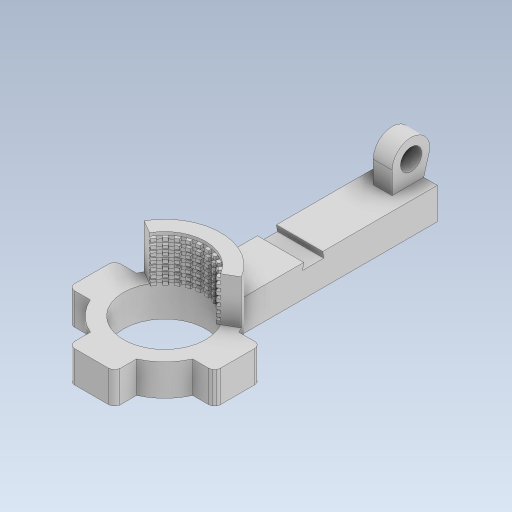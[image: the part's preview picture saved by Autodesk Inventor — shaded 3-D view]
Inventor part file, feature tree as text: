
AUTODESK INVENTOR PART (.ipt)
format: ipt  version: 2023 (Build 270158000, 158)  size: 567,808 bytes
history: native  units: in
note: dims shown in document units (in); Inventor stores cm internally (conversion verified against a paired STEP export)
features: sketch x10, extrude x8, revolve x1, hole x1, mirror x1, projected_geometry x1
ambient origin geometry x8: Origin, YZ Plane, XZ Plane, XY Plane, X Axis, Y Axis, Z Axis, Center Point
bodies: Solid1 (feature_tree)
feature tree (22):
  extrude  "Extrusion1"  Depth=0.3937in TaperAngle=0.0deg
  extrude  "Extrusion2"  Depth=0.5512in TaperAngle=0.0deg
  extrude  "Extrusion3"  Depth=0.0394in TaperAngle=120.0deg
  revolve  "Revolution1"  [1 undecoded]
  extrude  "Extrusion4"  Depth=0.1969in TaperAngle=0.0deg
  extrude  "Extrusion5"  Depth=0.2362in
  extrude  "Extrusion6"  Depth=0.0787in
  hole  "Hole1"  [1 undecoded]
  mirror  "Mirror1"
  extrude  "Extrusion7"  Depth=0.2756in
  extrude  "Extrusion8"  Depth=0.0787in
  sketch  "Sketch1"  dims[d0=1.0236in d1=0.3937in d2=0.0in]
  sketch  "Sketch2"  dims[d3=120.0deg d4=0.5512in d5=0.0in]
  sketch  "Sketch3"  dims[d6=0.0394in d7=7.874in d9=120.0deg]
  sketch  "Sketch4"  dims[d11=0.3937in d12=0.0in d14=5.5118in d16=0.0394in d17=0.3937in d19=0.3937in]
  sketch  "Sketch5"  dims[d21=360.0deg d22=2.2835in d23=0.1969in d24=0.0in d25=0.0in]
  sketch  "Sketch6"  dims[d26=0.2362in d27=1.4479in]
  sketch  "Sketch7"  dims[d28=1.3998in d29=0.0787in d30=0.0687in]
  sketch  "Sketch8"  dims[d31=0.2362in d32=0.4724in]
  sketch  "Sketch9"  dims[d33=0.5906in d34=0.0in d35=0.2756in]
  sketch  "Sketch10"  dims[d36=0.266in d37=0.2362in d38=0.1575in d39=0.0787in d40=90.0deg d41=0.315in d42=0.8108in d43=0.0787in d44=0.7874in d46=90.0deg d48=0.0in d49=0.0in d50=0.0787in d51=0.0in d52=0.0in]
  projected_geometry  "Projected Loop1"
note: 2 required parameter values undecoded (feature->parameter linkage not recoverable at this tier; creation-order binding heuristic only, values carry confidence <= 0.55)